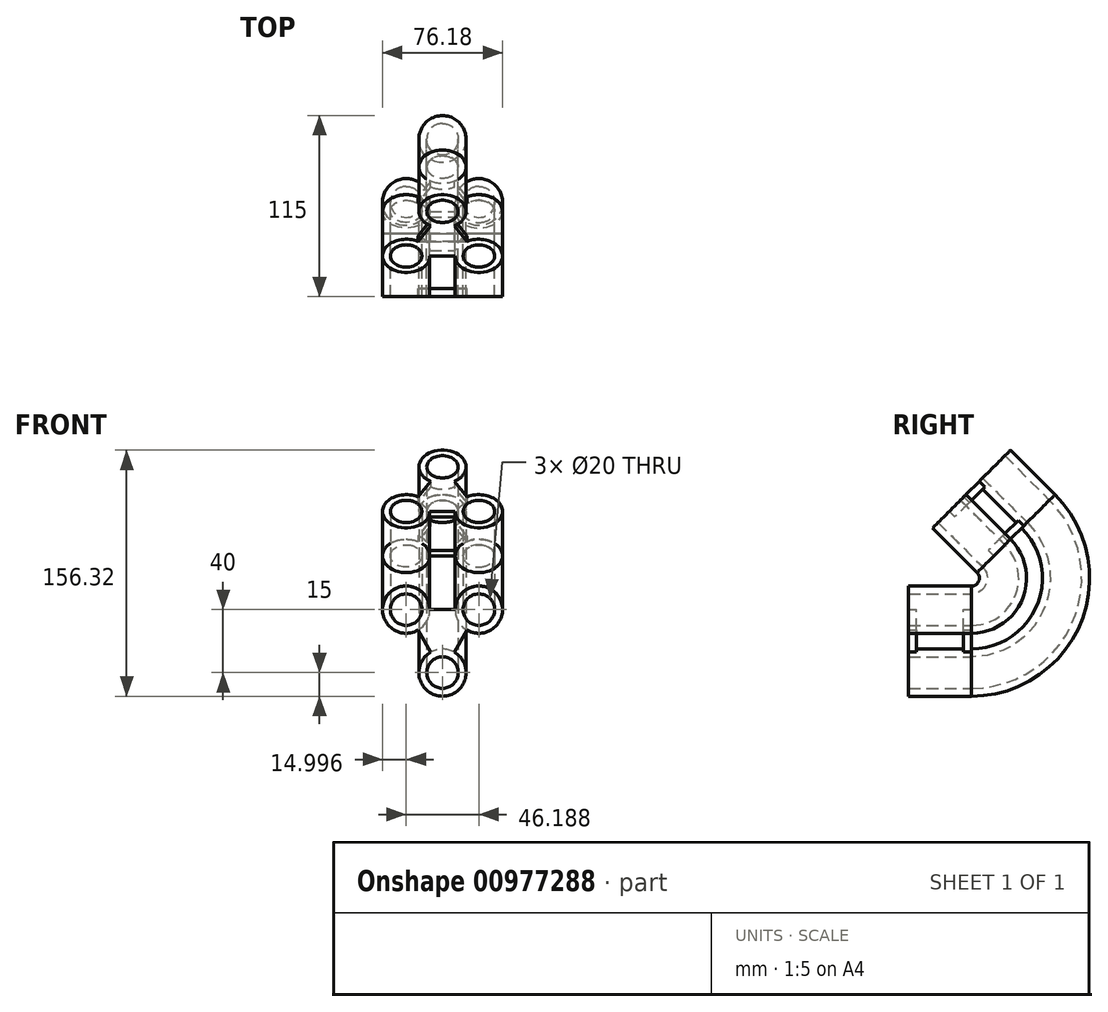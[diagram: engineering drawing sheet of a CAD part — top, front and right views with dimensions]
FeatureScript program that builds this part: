
annotation { "Feature Type Name" : "Feature", "Feature Type Description" : "" }
export const myFeature = defineFeature(function(context is Context, id is Id, definition is map)
    precondition{}
    {
        {
            var Q0;
            Q0=qCreatedBy(makeId("Front.planeOp"),FACE);
            var sketch = newSketch(context, id + "F0", { "sketchPlane" : qUnion([Q0])});
            skCircle(sketch, "E0", {"center": v(0, 0) * mm, "radius": 10 * mm});
            skCircle(sketch, "E1", {"center": v(23.1, 40) * mm, "radius": 10 * mm});
            skCircle(sketch, "E2", {"center": v(-23.1, 40) * mm, "radius": 10 * mm});
            skCircle(sketch, "E3", {"center": v(-23.1, 40) * mm, "radius": 15 * mm});
            skCircle(sketch, "E4", {"center": v(23.1, 40) * mm, "radius": 15 * mm});
            skCircle(sketch, "E5", {"center": v(0, 0) * mm, "radius": 15 * mm});
            skLineSegment(sketch, "E6", {"start": v(0, 0) * mm, "end": v(-23.1, 40) * mm});
            skLineSegment(sketch, "E7", {"start": v(23.1, 40) * mm, "end": v(0, 0) * mm});
            skLineSegment(sketch, "E8", {"start": v(-23.1, 40) * mm, "end": v(23.1, 40) * mm});
            skPoint(sketch, "E9", {"position": v(0, 40) * mm});
            skSolve(sketch);
        }
        {
            var Q0;
            Q0=qCreatedBy(makeId("Right.planeOp"),FACE);
            var sketch = newSketch(context, id + "F1", { "sketchPlane" : qUnion([Q0])});
            skArc(sketch, "E10", {"start": v(0, 40) * mm, "mid": v(18.48, 52.35) * mm, "end": v(14.14, 74.14) * mm});
            skLineSegment(sketch, "E11", {"start": v(14.14, 74.14) * mm, "end": v(0, 60) * mm});
            skLineSegment(sketch, "E12", {"start": v(0, 40) * mm, "end": v(0, 60) * mm});
            skSolve(sketch);
        }
        {
            var Q0;
            {var subQ0=sQuery(id+"F0.wireOp",EDGE,"E7");var subQ1=sQuery(id+"F0.wireOp",EDGE,"E1");var subQ2=makeQuery(id+"F0.imprint","INTERSECT",VERTEX,{"derivedFrom":[subQ1,subQ0]});Q0=makeQuery(id+"F0.imprint","IMPRINT",FACE,{"disambiguationData":[TD([[makeQuery(id+"F0.imprint","IMPRINT",EDGE,{"disambiguationData":[TD([[subQ2,-1.0]])],"derivedFrom":subQ1}),-1.0]])]});}
            var Q1;
            {var subQ0=sQuery(id+"F0.wireOp",EDGE,"E7");var subQ1=sQuery(id+"F0.wireOp",EDGE,"E1");var subQ2=makeQuery(id+"F0.imprint","INTERSECT",VERTEX,{"derivedFrom":[subQ1,subQ0]});Q1=makeQuery(id+"F0.imprint","IMPRINT",FACE,{"disambiguationData":[TD([[makeQuery(id+"F0.imprint","IMPRINT",EDGE,{"disambiguationData":[TD([[subQ2,1.0]])],"derivedFrom":subQ1}),-1.0]])]});}
            var Q2;
            {var subQ0=sQuery(id+"F0.wireOp",EDGE,"E6");var subQ1=sQuery(id+"F0.wireOp",EDGE,"E2");var subQ2=makeQuery(id+"F0.imprint","INTERSECT",VERTEX,{"derivedFrom":[subQ1,subQ0]});Q2=makeQuery(id+"F0.imprint","IMPRINT",FACE,{"disambiguationData":[TD([[makeQuery(id+"F0.imprint","IMPRINT",EDGE,{"disambiguationData":[TD([[subQ2,1.0]])],"derivedFrom":subQ1}),-1.0]])]});}
            var Q3;
            {var subQ0=sQuery(id+"F0.wireOp",EDGE,"E6");var subQ1=sQuery(id+"F0.wireOp",EDGE,"E2");var subQ2=makeQuery(id+"F0.imprint","INTERSECT",VERTEX,{"derivedFrom":[subQ1,subQ0]});Q3=makeQuery(id+"F0.imprint","IMPRINT",FACE,{"disambiguationData":[TD([[makeQuery(id+"F0.imprint","IMPRINT",EDGE,{"disambiguationData":[TD([[subQ2,-1.0]])],"derivedFrom":subQ1}),-1.0]])]});}
            var Q4;
            {var subQ0=sQuery(id+"F0.wireOp",EDGE,"E6");var subQ1=sQuery(id+"F0.wireOp",EDGE,"E0");var subQ2=makeQuery(id+"F0.imprint","INTERSECT",VERTEX,{"derivedFrom":[subQ1,subQ0]});Q4=makeQuery(id+"F0.imprint","IMPRINT",FACE,{"disambiguationData":[TD([[makeQuery(id+"F0.imprint","IMPRINT",EDGE,{"disambiguationData":[TD([[subQ2,-1.0]])],"derivedFrom":subQ1}),-1.0]])]});}
            var Q5;
            {var subQ0=sQuery(id+"F0.wireOp",EDGE,"E6");var subQ1=sQuery(id+"F0.wireOp",EDGE,"E0");var subQ2=makeQuery(id+"F0.imprint","INTERSECT",VERTEX,{"derivedFrom":[subQ1,subQ0]});Q5=makeQuery(id+"F0.imprint","IMPRINT",FACE,{"disambiguationData":[TD([[makeQuery(id+"F0.imprint","IMPRINT",EDGE,{"disambiguationData":[TD([[subQ2,1.0]])],"derivedFrom":subQ1}),-1.0]])]});}
            var Q6;
            Q6=sQuery(id+"F1.wireOp",EDGE,"E10");
            sweep(context, id + "F2", {"profiles" : qUnion([Q0, Q1, Q2, Q3, Q4, Q5]), "path" : qUnion([Q6])});
        }
        {
            var Q0;
            {var subQ0=sQuery(id+"F0.wireOp",EDGE,"E6");var subQ1=sQuery(id+"F0.wireOp",EDGE,"E2");var subQ2=makeQuery(id+"F0.imprint","INTERSECT",VERTEX,{"derivedFrom":[subQ1,subQ0]});Q0=makeQuery(id+"F0.imprint","IMPRINT",FACE,{"disambiguationData":[TD([[makeQuery(id+"F0.imprint","IMPRINT",EDGE,{"disambiguationData":[TD([[subQ2,1.0]])],"derivedFrom":subQ1}),-1.0]])]});}
            var Q1;
            {var subQ0=sQuery(id+"F0.wireOp",EDGE,"E6");var subQ1=sQuery(id+"F0.wireOp",EDGE,"E2");var subQ2=makeQuery(id+"F0.imprint","INTERSECT",VERTEX,{"derivedFrom":[subQ1,subQ0]});Q1=makeQuery(id+"F0.imprint","IMPRINT",FACE,{"disambiguationData":[TD([[makeQuery(id+"F0.imprint","IMPRINT",EDGE,{"disambiguationData":[TD([[subQ2,-1.0]])],"derivedFrom":subQ1}),-1.0]])]});}
            var Q2;
            {var subQ0=sQuery(id+"F0.wireOp",EDGE,"E6");var subQ1=sQuery(id+"F0.wireOp",EDGE,"E3");var subQ2=makeQuery(id+"F0.imprint","INTERSECT",VERTEX,{"derivedFrom":[subQ1,subQ0]});Q2=makeQuery(id+"F0.imprint","IMPRINT",FACE,{"disambiguationData":[TD([[makeQuery(id+"F0.imprint","IMPRINT",EDGE,{"disambiguationData":[TD([[subQ2,-1.0]])],"derivedFrom":subQ1}),-1.0]])]});}
            var Q3;
            {var subQ0=sQuery(id+"F0.wireOp",EDGE,"E7");var subQ1=sQuery(id+"F0.wireOp",EDGE,"E1");var subQ2=makeQuery(id+"F0.imprint","INTERSECT",VERTEX,{"derivedFrom":[subQ1,subQ0]});Q3=makeQuery(id+"F0.imprint","IMPRINT",FACE,{"disambiguationData":[TD([[makeQuery(id+"F0.imprint","IMPRINT",EDGE,{"disambiguationData":[TD([[subQ2,1.0]])],"derivedFrom":subQ1}),-1.0]])]});}
            var Q4;
            {var subQ0=sQuery(id+"F0.wireOp",EDGE,"E7");var subQ1=sQuery(id+"F0.wireOp",EDGE,"E1");var subQ2=makeQuery(id+"F0.imprint","INTERSECT",VERTEX,{"derivedFrom":[subQ1,subQ0]});Q4=makeQuery(id+"F0.imprint","IMPRINT",FACE,{"disambiguationData":[TD([[makeQuery(id+"F0.imprint","IMPRINT",EDGE,{"disambiguationData":[TD([[subQ2,-1.0]])],"derivedFrom":subQ1}),-1.0]])]});}
            var Q5;
            {var subQ0=sQuery(id+"F0.wireOp",EDGE,"E6");var subQ1=sQuery(id+"F0.wireOp",EDGE,"E0");var subQ2=makeQuery(id+"F0.imprint","INTERSECT",VERTEX,{"derivedFrom":[subQ1,subQ0]});Q5=makeQuery(id+"F0.imprint","IMPRINT",FACE,{"disambiguationData":[TD([[makeQuery(id+"F0.imprint","IMPRINT",EDGE,{"disambiguationData":[TD([[subQ2,1.0]])],"derivedFrom":subQ1}),-1.0]])]});}
            var Q6;
            {var subQ0=sQuery(id+"F0.wireOp",EDGE,"E6");var subQ1=sQuery(id+"F0.wireOp",EDGE,"E0");var subQ2=makeQuery(id+"F0.imprint","INTERSECT",VERTEX,{"derivedFrom":[subQ1,subQ0]});Q6=makeQuery(id+"F0.imprint","IMPRINT",FACE,{"disambiguationData":[TD([[makeQuery(id+"F0.imprint","IMPRINT",EDGE,{"disambiguationData":[TD([[subQ2,-1.0]])],"derivedFrom":subQ1}),-1.0]])]});}
            extrude(context, id + "F3", {"entities" : qUnion([Q0, Q1, Q2, Q3, Q4, Q5, Q6]), "depth" : 40 * mm, "offsetDistance" : 25 * mm});
        }
        {
            var Q0;
            Q0=makeQuery(id+"F2.opSweep","CAP_FACE",FACE,{"disambiguationData":[OSD([sQuery(id+"F0.wireOp",EDGE,"E3"),sQuery(id+"F1.wireOp",VERTEX,"E10.end")])],"isStart":false});
            var sketch = newSketch(context, id + "F4", { "sketchPlane" : qUnion([Q0])});
            skCircle(sketch, "E13", {"center": v(-23.1, 62.43) * mm, "radius": 15 * mm});
            skCircle(sketch, "E14", {"center": v(23.1, 62.43) * mm, "radius": 15 * mm});
            skCircle(sketch, "E15", {"center": v(0, 102.43) * mm, "radius": 15 * mm});
            skLineSegment(sketch, "E16", {"start": v(-23.1, 62.43) * mm, "end": v(23.1, 62.43) * mm});
            skLineSegment(sketch, "E17", {"start": v(23.1, 62.43) * mm, "end": v(0, 102.43) * mm});
            skLineSegment(sketch, "E18", {"start": v(0, 102.43) * mm, "end": v(-23.1, 62.43) * mm});
            skCircle(sketch, "E19", {"center": v(-23.1, 62.43) * mm, "radius": 10 * mm});
            skCircle(sketch, "E20", {"center": v(0, 102.43) * mm, "radius": 10 * mm});
            skCircle(sketch, "E21", {"center": v(23.1, 62.43) * mm, "radius": 10 * mm});
            skSolve(sketch);
        }
        {
            var Q0;
            Q0=qSketchRegion(id+"F4",true);
            extrude(context, id + "F5", {"entities" : qUnion([Q0]), "depth" : 40 * mm, "offsetDistance" : 25 * mm});
        }
        {
            var Q0;
            Q0=qSketchRegion(id+"F4",true);
            extrude(context, id + "F6", {"entities" : qUnion([Q0]), "depth" : 40 * mm, "offsetDistance" : 25 * mm});
        }
        {
            var Q0;
            {var subQ0=sQuery(id+"F0.wireOp",EDGE,"E6");var subQ1=sQuery(id+"F0.wireOp",EDGE,"E3");var subQ2=makeQuery(id+"F0.imprint","INTERSECT",VERTEX,{"derivedFrom":[subQ1,subQ0]});Q0=makeQuery(id+"F0.imprint","IMPRINT",FACE,{"disambiguationData":[TD([[makeQuery(id+"F0.imprint","IMPRINT",EDGE,{"disambiguationData":[TD([[subQ2,-1.0]])],"derivedFrom":subQ1}),-1.0]])]});}
            extrude(context, id + "F7", {"entities" : qUnion([Q0]), "operationType" : NewBodyOperationType.REMOVE, "depth" : 35 * mm, "offsetDistance" : 25 * mm, "hasSecondDirection" : true, "secondDirectionOppositeDirection" : false, "secondDirectionDepth" : 5 * mm});
        }
        {
            var Q0;
            {var subQ0=sQuery(id+"F4.wireOp",EDGE,"E16");var subQ1=sQuery(id+"F4.wireOp",EDGE,"E13");var subQ2=makeQuery(id+"F4.imprint","INTERSECT",VERTEX,{"derivedFrom":[subQ1,subQ0]});Q0=makeQuery(id+"F4.imprint","IMPRINT",FACE,{"disambiguationData":[TD([[makeQuery(id+"F4.imprint","IMPRINT",EDGE,{"disambiguationData":[TD([[subQ2,1.0]])],"derivedFrom":subQ1}),1.0]])]});}
            extrude(context, id + "F8", {"entities" : qUnion([Q0]), "operationType" : NewBodyOperationType.REMOVE, "depth" : 35 * mm, "offsetDistance" : 25 * mm, "hasSecondDirection" : true, "secondDirectionOppositeDirection" : false, "secondDirectionDepth" : 5 * mm});
        }
    });
